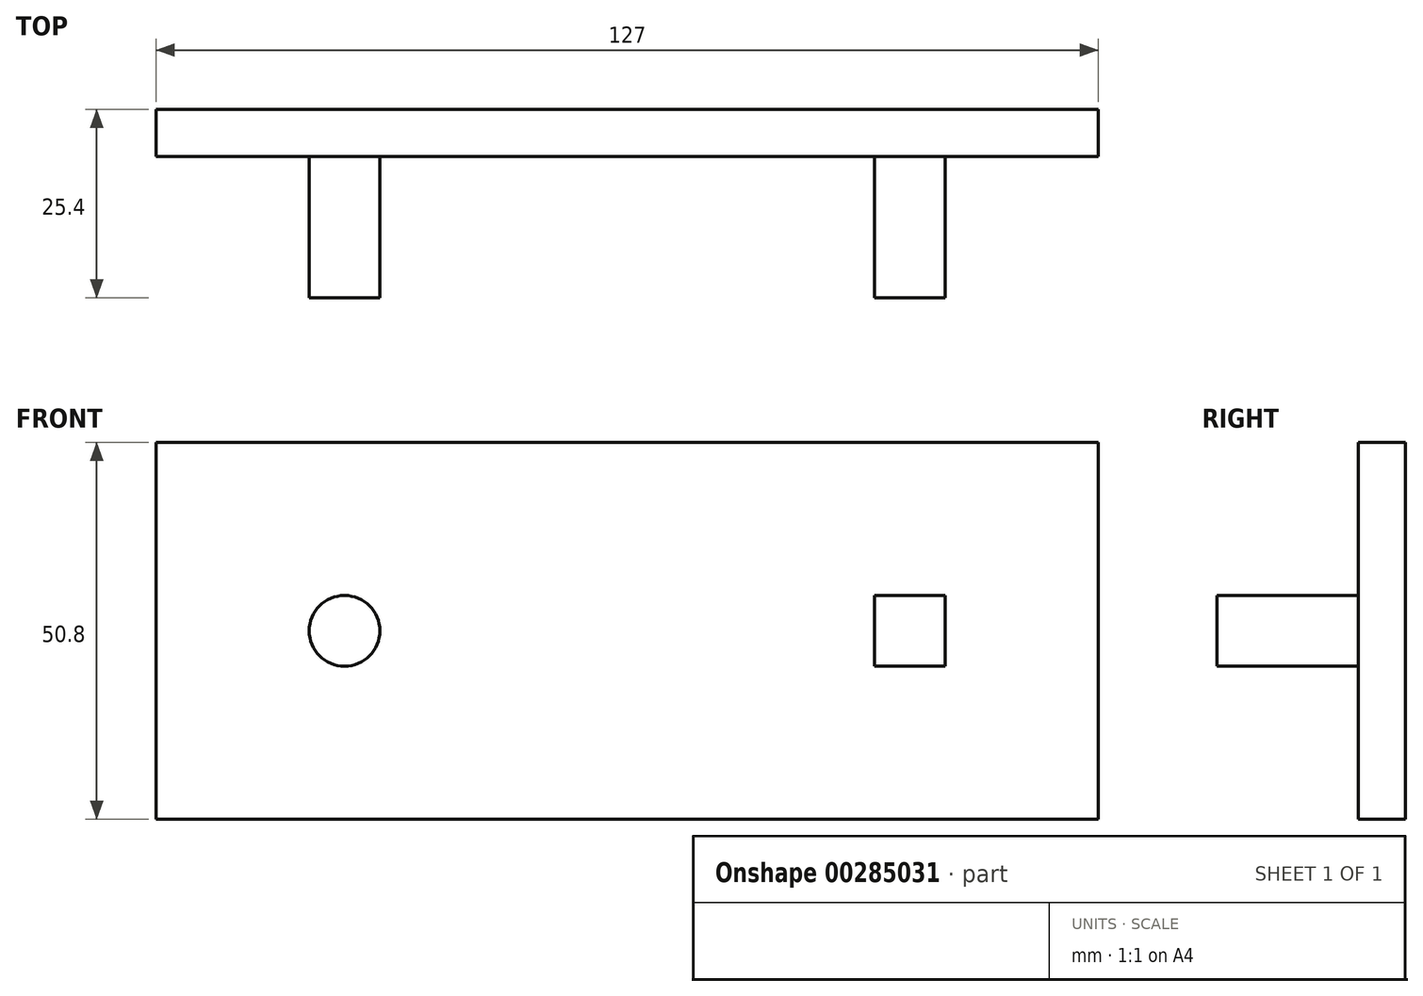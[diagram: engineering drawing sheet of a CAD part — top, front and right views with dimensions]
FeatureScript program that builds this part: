
annotation { "Feature Type Name" : "Feature", "Feature Type Description" : "" }
export const myFeature = defineFeature(function(context is Context, id is Id, definition is map)
    precondition{}
    {
        {
            var Q0;
            Q0=qCreatedBy(makeId("Front.planeOp"),FACE);
            var sketch = newSketch(context, id + "F0", { "sketchPlane" : qUnion([Q0])});
            skLineSegment(sketch, "E0.bottom", {"start": v(63.5, -25.4) * mm, "end": v(-63.5, -25.4) * mm});
            skLineSegment(sketch, "E0.top", {"start": v(63.5, 25.4) * mm, "end": v(-63.5, 25.4) * mm});
            skLineSegment(sketch, "E0.left", {"start": v(63.5, -25.4) * mm, "end": v(63.5, 25.4) * mm});
            skLineSegment(sketch, "E0.right", {"start": v(-63.5, -25.4) * mm, "end": v(-63.5, 25.4) * mm});
            skPoint(sketch, "E0.middle", {"position": v(0, 0) * mm});
            skCircle(sketch, "E1", {"center": v(-38.1, 0) * mm, "radius": 4.76 * mm});
            skLineSegment(sketch, "E2.bottom", {"start": v(42.86, -4.76) * mm, "end": v(33.34, -4.76) * mm});
            skLineSegment(sketch, "E2.top", {"start": v(42.86, 4.76) * mm, "end": v(33.34, 4.76) * mm});
            skLineSegment(sketch, "E2.left", {"start": v(42.86, -4.76) * mm, "end": v(42.86, 4.76) * mm});
            skLineSegment(sketch, "E2.right", {"start": v(33.34, -4.76) * mm, "end": v(33.34, 4.76) * mm});
            skPoint(sketch, "E2.middle", {"position": v(38.1, 0) * mm});
            skSolve(sketch);
        }
        {
            var Q0;
            Q0=makeQuery(id+"F0.imprint","IMPRINT",FACE,{"disambiguationData":[TD([[makeQuery(id+"F0.imprint","IMPRINT",EDGE,{"derivedFrom":sQuery(id+"F0.wireOp",EDGE,"E0.bottom")}),-1.0]])]});
            var Q1;
            Q1=makeQuery(id+"F0.imprint","IMPRINT",FACE,{"disambiguationData":[TD([[makeQuery(id+"F0.imprint","IMPRINT",EDGE,{"derivedFrom":sQuery(id+"F0.wireOp",EDGE,"E1")}),1.0]])]});
            var Q2;
            Q2=makeQuery(id+"F0.imprint","IMPRINT",FACE,{"disambiguationData":[TD([[makeQuery(id+"F0.imprint","IMPRINT",EDGE,{"derivedFrom":sQuery(id+"F0.wireOp",EDGE,"E2.bottom")}),-1.0]])]});
            extrude(context, id + "F1", {"entities" : qUnion([Q0, Q1, Q2]), "depth" : 6.35 * mm});
        }
        {
            var Q0;
            Q0=makeQuery(id+"F0.imprint","IMPRINT",FACE,{"disambiguationData":[TD([[makeQuery(id+"F0.imprint","IMPRINT",EDGE,{"derivedFrom":sQuery(id+"F0.wireOp",EDGE,"E2.bottom")}),-1.0]])]});
            var Q1;
            Q1=makeQuery(id+"F0.imprint","IMPRINT",FACE,{"disambiguationData":[TD([[makeQuery(id+"F0.imprint","IMPRINT",EDGE,{"derivedFrom":sQuery(id+"F0.wireOp",EDGE,"E1")}),1.0]])]});
            extrude(context, id + "F2", {"entities" : qUnion([Q0, Q1]), "operationType" : NewBodyOperationType.ADD, "depth" : 25.4 * mm});
        }
    });
